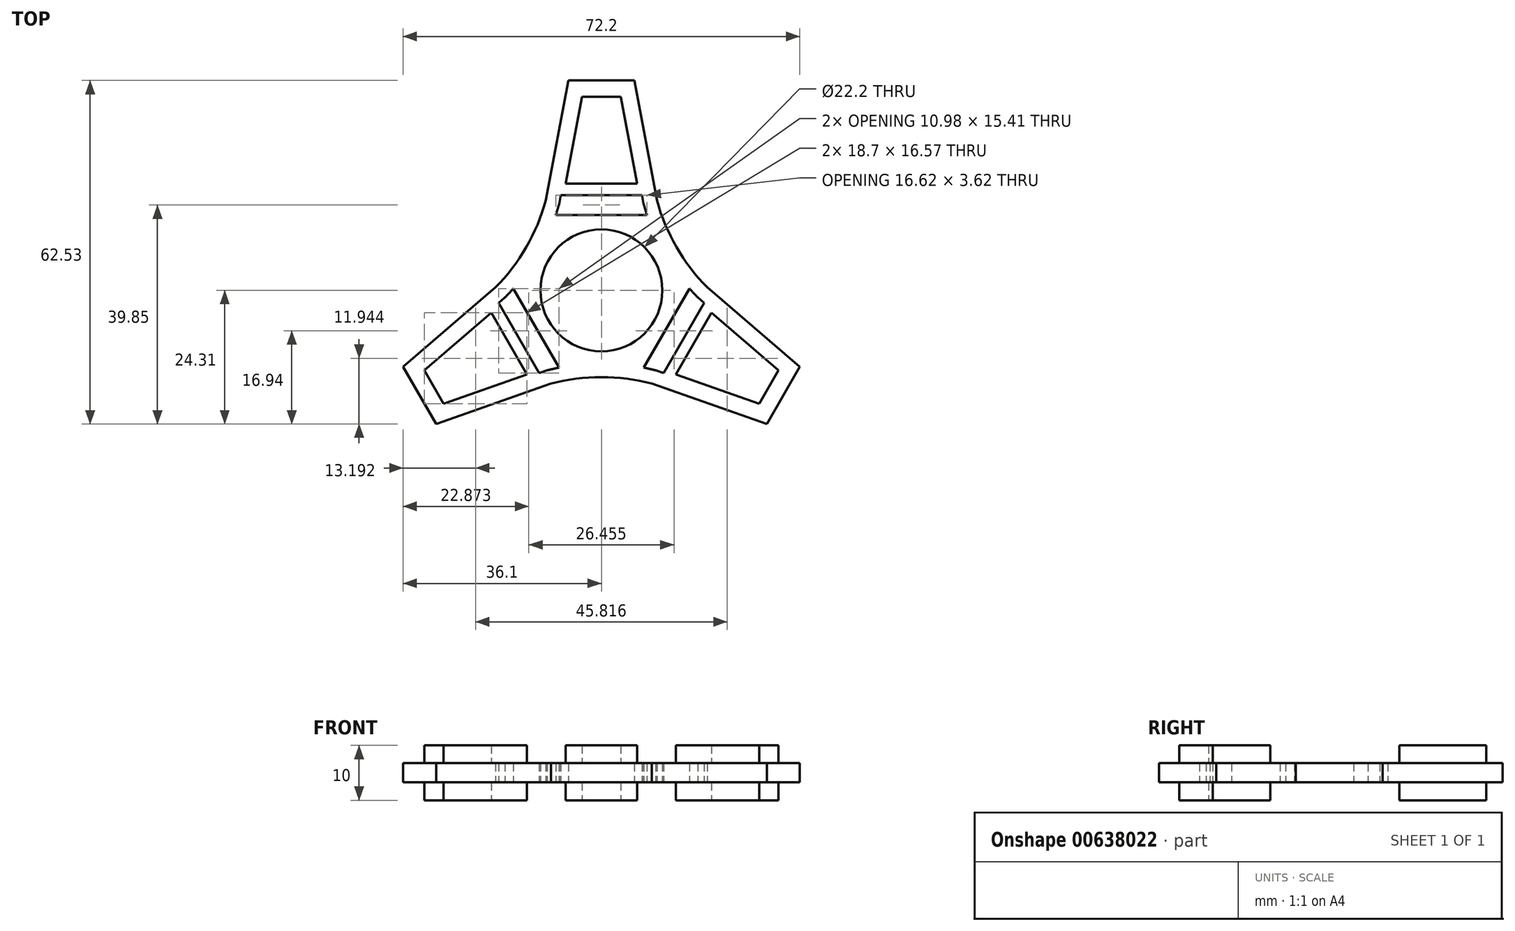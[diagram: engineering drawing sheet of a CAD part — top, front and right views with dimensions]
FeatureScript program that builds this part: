
annotation { "Feature Type Name" : "Feature", "Feature Type Description" : "" }
export const myFeature = defineFeature(function(context is Context, id is Id, definition is map)
    precondition{}
    {
        {
            var Q0;
            Q0=qCreatedBy(makeId("Top.planeOp"),FACE);
            var sketch = newSketch(context, id + "F0", { "sketchPlane" : qUnion([Q0])});
            skCircle(sketch, "E0", {"center": v(0, 0) * mm, "radius": 11.1 * mm});
            skLineSegment(sketch, "E1", {"start": v(0, 38.22) * mm, "end": v(6, 38.22) * mm});
            skLineSegment(sketch, "E2", {"start": v(6, 38.22) * mm, "end": v(0, 38.22) * mm});
            skLineSegment(sketch, "E3", {"start": v(-6, 38.22) * mm, "end": v(0, 38.22) * mm});
            skLineSegment(sketch, "E4", {"start": v(-6, 38.22) * mm, "end": v(-10.1, 16.4) * mm});
            skLineSegment(sketch, "E5.MirrorCS", {"start": v(6, 38.22) * mm, "end": v(10.1, 16.4) * mm});
            skPoint(sketch, "E6.center", {"position": v(-0.5, -1.62) * mm});
            skArc(sketch, "E7", {"start": v(-19.26, 0.55) * mm, "mid": v(-13.67, 7.89) * mm, "end": v(-10.1, 16.4) * mm});
            skPoint(sketch, "E8.0.center.orphan", {"position": v(3.7, -1.78) * mm});
            skArc(sketch, "E9.1.0", {"start": v(9.15, -16.96) * mm, "mid": v(0, -15.78) * mm, "end": v(-9.15, -16.96) * mm});
            skArc(sketch, "E9.2.0", {"start": v(10.1, 16.4) * mm, "mid": v(13.67, 7.89) * mm, "end": v(19.26, 0.55) * mm});
            skLineSegment(sketch, "E10.1.0", {"start": v(-30.1, -24.3) * mm, "end": v(-9.15, -16.96) * mm});
            skLineSegment(sketch, "E10.1.1", {"start": v(-30.1, -24.3) * mm, "end": v(-33.1, -19.1) * mm});
            skLineSegment(sketch, "E10.1.2", {"start": v(-36.1, -13.91) * mm, "end": v(-33.1, -19.1) * mm});
            skLineSegment(sketch, "E10.1.3", {"start": v(-36.1, -13.91) * mm, "end": v(-19.26, 0.55) * mm});
            skLineSegment(sketch, "E10.2.0", {"start": v(36.1, -13.91) * mm, "end": v(19.26, 0.55) * mm});
            skLineSegment(sketch, "E10.2.1", {"start": v(36.1, -13.91) * mm, "end": v(33.1, -19.1) * mm});
            skLineSegment(sketch, "E10.2.2", {"start": v(30.1, -24.3) * mm, "end": v(33.1, -19.1) * mm});
            skLineSegment(sketch, "E10.2.3", {"start": v(30.1, -24.3) * mm, "end": v(9.15, -16.96) * mm});
            skPoint(sketch, "E11.orphan", {"position": v(-21.4, -1.45) * mm});
            skPoint(sketch, "E12.orphan", {"position": v(11.96, -17.82) * mm});
            skPoint(sketch, "E13.orphan", {"position": v(9.45, 19.27) * mm});
            skLineSegment(sketch, "E14.0", {"start": v(-6.5, 19.4) * mm, "end": v(6.5, 19.4) * mm});
            skLineSegment(sketch, "E14.1", {"start": v(-3.51, 35.22) * mm, "end": v(-6.5, 19.4) * mm});
            skLineSegment(sketch, "E14.2", {"start": v(3.51, 35.22) * mm, "end": v(6.5, 19.4) * mm});
            skLineSegment(sketch, "E14.3", {"start": v(3.51, 35.22) * mm, "end": v(0, 35.22) * mm});
            skLineSegment(sketch, "E14.4", {"start": v(-3.51, 35.22) * mm, "end": v(0, 35.22) * mm});
            skArc(sketch, "E15.0", {"start": v(-8.31, 13.73) * mm, "mid": v(-7.98, 14.78) * mm, "end": v(-7.67, 15.84) * mm});
            skLineSegment(sketch, "E15.1", {"start": v(-7.39, 17.35) * mm, "end": v(-7.67, 15.84) * mm});
            skArc(sketch, "E16.0", {"start": v(7.67, 15.84) * mm, "mid": v(7.98, 14.78) * mm, "end": v(8.31, 13.73) * mm});
            skLineSegment(sketch, "E16.1", {"start": v(7.39, 17.35) * mm, "end": v(7.67, 15.84) * mm});
            skLineSegment(sketch, "E17", {"start": v(-7.39, 17.35) * mm, "end": v(7.39, 17.35) * mm});
            skLineSegment(sketch, "E18", {"start": v(-8.31, 13.73) * mm, "end": v(8.31, 13.73) * mm});
            skLineSegment(sketch, "E19.1.0", {"start": v(-32.26, -14.57) * mm, "end": v(-20.05, -4.08) * mm});
            skLineSegment(sketch, "E19.1.1", {"start": v(-32.26, -14.57) * mm, "end": v(-30.5, -17.6) * mm});
            skLineSegment(sketch, "E19.1.2", {"start": v(-28.74, -20.65) * mm, "end": v(-30.5, -17.6) * mm});
            skLineSegment(sketch, "E19.1.3", {"start": v(-28.74, -20.65) * mm, "end": v(-13.56, -15.32) * mm});
            skLineSegment(sketch, "E19.1.4", {"start": v(-13.56, -15.32) * mm, "end": v(-20.05, -4.08) * mm});
            skLineSegment(sketch, "E19.2.0", {"start": v(28.74, -20.65) * mm, "end": v(13.56, -15.32) * mm});
            skLineSegment(sketch, "E19.2.1", {"start": v(28.74, -20.65) * mm, "end": v(30.5, -17.6) * mm});
            skLineSegment(sketch, "E19.2.2", {"start": v(32.26, -14.57) * mm, "end": v(30.5, -17.6) * mm});
            skLineSegment(sketch, "E19.2.3", {"start": v(32.26, -14.57) * mm, "end": v(20.05, -4.08) * mm});
            skLineSegment(sketch, "E19.2.4", {"start": v(20.05, -4.08) * mm, "end": v(13.56, -15.32) * mm});
            skLineSegment(sketch, "E20.1.0", {"start": v(-11.33, -15.07) * mm, "end": v(-18.72, -2.28) * mm});
            skLineSegment(sketch, "E20.1.1", {"start": v(-18.72, -2.28) * mm, "end": v(-17.56, -1.28) * mm});
            skArc(sketch, "E20.1.2", {"start": v(-17.56, -1.28) * mm, "mid": v(-16.79, -0.48) * mm, "end": v(-16.05, 0.33) * mm});
            skLineSegment(sketch, "E20.1.3", {"start": v(-7.74, -14.06) * mm, "end": v(-16.05, 0.33) * mm});
            skArc(sketch, "E20.1.4", {"start": v(-7.74, -14.06) * mm, "mid": v(-8.81, -14.3) * mm, "end": v(-9.89, -14.57) * mm});
            skLineSegment(sketch, "E20.1.5", {"start": v(-11.33, -15.07) * mm, "end": v(-9.89, -14.57) * mm});
            skLineSegment(sketch, "E20.2.0", {"start": v(18.72, -2.28) * mm, "end": v(11.33, -15.07) * mm});
            skLineSegment(sketch, "E20.2.1", {"start": v(11.33, -15.07) * mm, "end": v(9.89, -14.57) * mm});
            skArc(sketch, "E20.2.2", {"start": v(9.89, -14.57) * mm, "mid": v(8.81, -14.3) * mm, "end": v(7.74, -14.06) * mm});
            skLineSegment(sketch, "E20.2.3", {"start": v(16.05, 0.33) * mm, "end": v(7.74, -14.06) * mm});
            skArc(sketch, "E20.2.4", {"start": v(16.05, 0.33) * mm, "mid": v(16.79, -0.48) * mm, "end": v(17.56, -1.28) * mm});
            skLineSegment(sketch, "E20.2.5", {"start": v(18.72, -2.28) * mm, "end": v(17.56, -1.28) * mm});
            skSolve(sketch);
        }
        {
            var Q0;
            Q0=makeQuery(id+"F0.imprint","IMPRINT",FACE,{"disambiguationData":[TD([[makeQuery(id+"F0.imprint","IMPRINT",EDGE,{"derivedFrom":sQuery(id+"F0.wireOp",EDGE,"E0")}),-1.0]])]});
            extrude(context, id + "F1", {"entities" : qUnion([Q0]), "endBound" : BoundingType.SYMMETRIC, "depth" : 3.5 * mm, "offsetDistance" : 25 * mm});
        }
        {
            var Q0;
            Q0=makeQuery(id+"F0.imprint","IMPRINT",FACE,{"disambiguationData":[TD([[makeQuery(id+"F0.imprint","IMPRINT",EDGE,{"derivedFrom":sQuery(id+"F0.wireOp",EDGE,"E19.2.0")}),-1.0]])]});
            var Q1;
            Q1=makeQuery(id+"F0.imprint","IMPRINT",FACE,{"disambiguationData":[TD([[makeQuery(id+"F0.imprint","IMPRINT",EDGE,{"derivedFrom":sQuery(id+"F0.wireOp",EDGE,"E14.0")}),1.0]])]});
            var Q2;
            Q2=makeQuery(id+"F0.imprint","IMPRINT",FACE,{"disambiguationData":[TD([[makeQuery(id+"F0.imprint","IMPRINT",EDGE,{"derivedFrom":sQuery(id+"F0.wireOp",EDGE,"E19.1.0")}),-1.0]])]});
            extrude(context, id + "F2", {"entities" : qUnion([Q0, Q1, Q2]), "operationType" : NewBodyOperationType.ADD, "endBound" : BoundingType.SYMMETRIC, "depth" : 10 * mm, "offsetDistance" : 25 * mm});
        }
    });
